# Revit family: 56 Intersan Saniwave Rx LRHD
name_source: partatom
category: Plumbing Fixtures
revit_build: Autodesk Revit 2017 (Build: 20170816_0615(x64)
units: mm (PartAtom-declared; Revit-internal decimal feet)

## family parameters
Always vertical = Yes
Cut with Voids When Loaded = No
OmniClass Number = 23.45.05.14.14
OmniClass Title = Sinks/Lavatories
Part Type = Normal
Room Calculation Point = No
Round Connector Dimension = Use Diameter
Shared = No
Work Plane-Based = No

## types (1)
- LRHD
    CW Connection = Yes
    Drain Diameter = 0"
    HW Connection = Yes
    Manufacturer = Intersan
    Material = Anti-microbial Solid Surface and Powder Coated Steel
    Model = Saniwave Rx
    Standard Conformance = CSA B45.5-11/IAPMO Z124-2011 - IAPMO IGC156
    Supply Cold Diameter = 1/2"
    Supply Hot Diameter = 1/2"
    Unit Depth = 22 1/4"
    Unit Height = 19"
    Unit Width = 20 1/4"
    Warranty = 5 years on material - 1 year on faucets
    Waste Connection = Yes
    Water Usage = 0.5 gpm

## geometry (parser evidence)
native form markers: Sweep x3
no freeform markers — native parametric forms only
